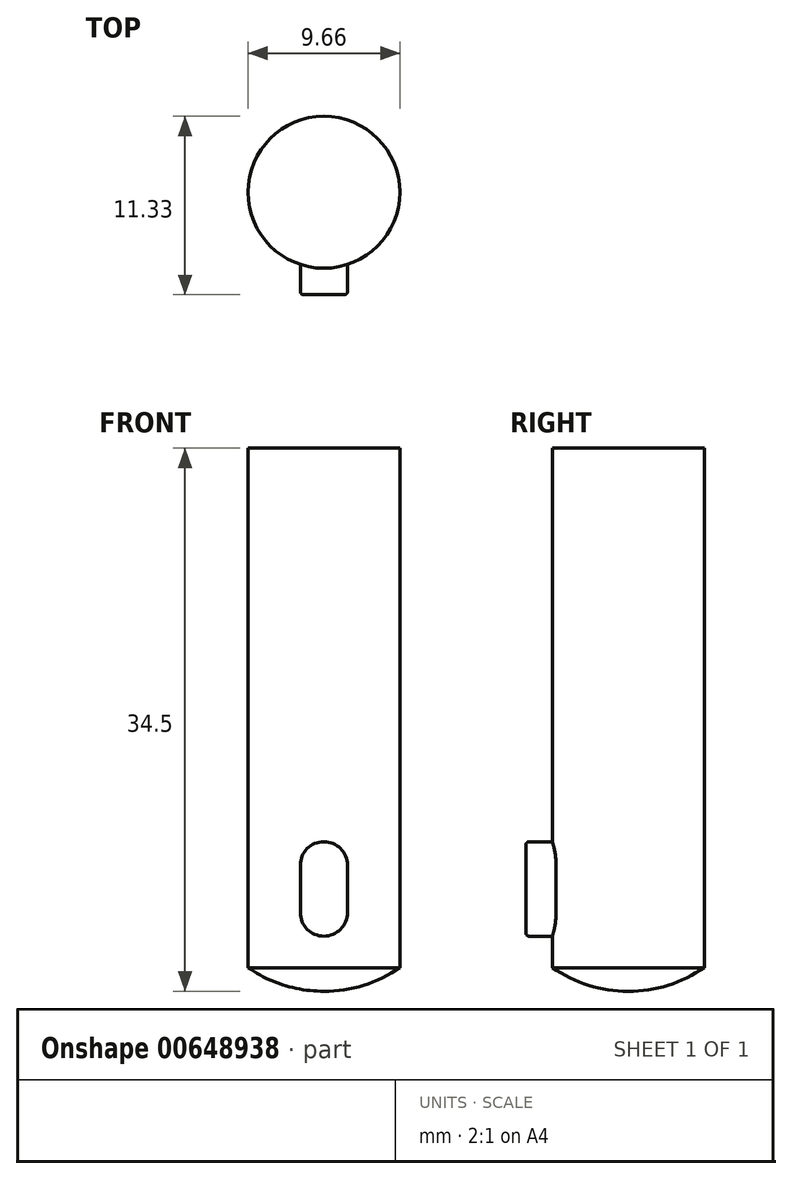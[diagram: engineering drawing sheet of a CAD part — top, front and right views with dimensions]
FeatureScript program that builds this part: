
annotation { "Feature Type Name" : "Feature", "Feature Type Description" : "" }
export const myFeature = defineFeature(function(context is Context, id is Id, definition is map)
    precondition{}
    {
        {
            var Q0;
            Q0=qCreatedBy(makeId("Top.planeOp"),FACE);
            var sketch = newSketch(context, id + "F0", { "sketchPlane" : qUnion([Q0])});
            skCircle(sketch, "E0", {"center": v(0, 0) * mm, "radius": 4.83 * mm});
            skSolve(sketch);
        }
        {
            var Q0;
            Q0=qSketchRegion(id+"F0",true);
            extrude(context, id + "F1", {"entities" : qUnion([Q0]), "depth" : 33 * mm});
        }
        {
            var Q0;
            Q0=qCreatedBy(makeId("Front.planeOp"),FACE);
            var sketch = newSketch(context, id + "F2", { "sketchPlane" : qUnion([Q0])});
            skLineSegment(sketch, "E1", {"start": v(0, 3.5) * mm, "end": v(0, 6.5) * mm, "construction": true});
            skArc(sketch, "E2.0.startCap", {"start": v(1.5, 3.5) * mm, "mid": v(0, 2) * mm, "end": v(-1.5, 3.5) * mm});
            skArc(sketch, "E2.0.endCap", {"start": v(-1.5, 6.5) * mm, "mid": v(0, 8) * mm, "end": v(1.5, 6.5) * mm});
            skLineSegment(sketch, "E2.0.left", {"start": v(-1.5, 3.5) * mm, "end": v(-1.5, 6.5) * mm});
            skLineSegment(sketch, "E2.0.right", {"start": v(1.5, 3.5) * mm, "end": v(1.5, 6.5) * mm});
            skSolve(sketch);
        }
        {
            var Q0;
            Q0=qSketchRegion(id+"F2",true);
            var Q1;
            Q1=qBodyType(qCreatedBy(id+"F2",EDGE),BodyType.WIRE);
            extrude(context, id + "F3", {"entities" : qUnion([Q0]), "operationType" : NewBodyOperationType.ADD, "surfaceEntities" : qUnion([Q1]), "depth" : 6.5 * mm});
        }
        {
            var Q0;
            Q0=makeQuery(id+"F3.opExtrude","CAP_FACE",FACE,{"disambiguationData":[OSD([sQuery(id+"F2.wireOp",EDGE,"E2.0.startCap"),sQuery(id+"F2.wireOp",EDGE,"E2.0.endCap"),sQuery(id+"F2.wireOp",EDGE,"E2.0.left"),sQuery(id+"F2.wireOp",EDGE,"E2.0.right")])],"isStart":false});
            fillet(context, id + "F4", {"entities" : qUnion([Q0]), "radius" : 0.2 * mm, "tangentPropagation" : true, "allowEdgeOverflow" : false});
        }
        {
            var Q0;
            Q0=qCreatedBy(makeId("Front.planeOp"),FACE);
            var sketch = newSketch(context, id + "F5", { "sketchPlane" : qUnion([Q0])});
            skLineSegment(sketch, "E3", {"start": v(0, 0) * mm, "end": v(0, -2.82) * mm, "construction": true});
            skLineSegment(sketch, "E4", {"start": v(-4.62, -1.5) * mm, "end": v(4.9, -1.5) * mm, "construction": true});
            skLineSegment(sketch, "E5.0", {"start": v(-4.83, 0) * mm, "end": v(0, 0) * mm});
            skArc(sketch, "E6", {"start": v(-4.83, 0) * mm, "mid": v(-2.53, -1.12) * mm, "end": v(0, -1.5) * mm});
            skLineSegment(sketch, "E7", {"start": v(0, 0) * mm, "end": v(0, -1.5) * mm});
            skPoint(sketch, "E8.orphan", {"position": v(4.83, 0) * mm});
            skSolve(sketch);
        }
        {
            var Q0;
            Q0=qSketchRegion(id+"F5",true);
            var Q1;
            Q1=sQuery(id+"F5.wireOp",EDGE,"E3");
            revolve(context, id + "F6", {"operationType" : NewBodyOperationType.ADD, "entities" : qUnion([Q0]), "axis" : qUnion([Q1]), "revolveType" : RevolveType.FULL});
        }
    });
